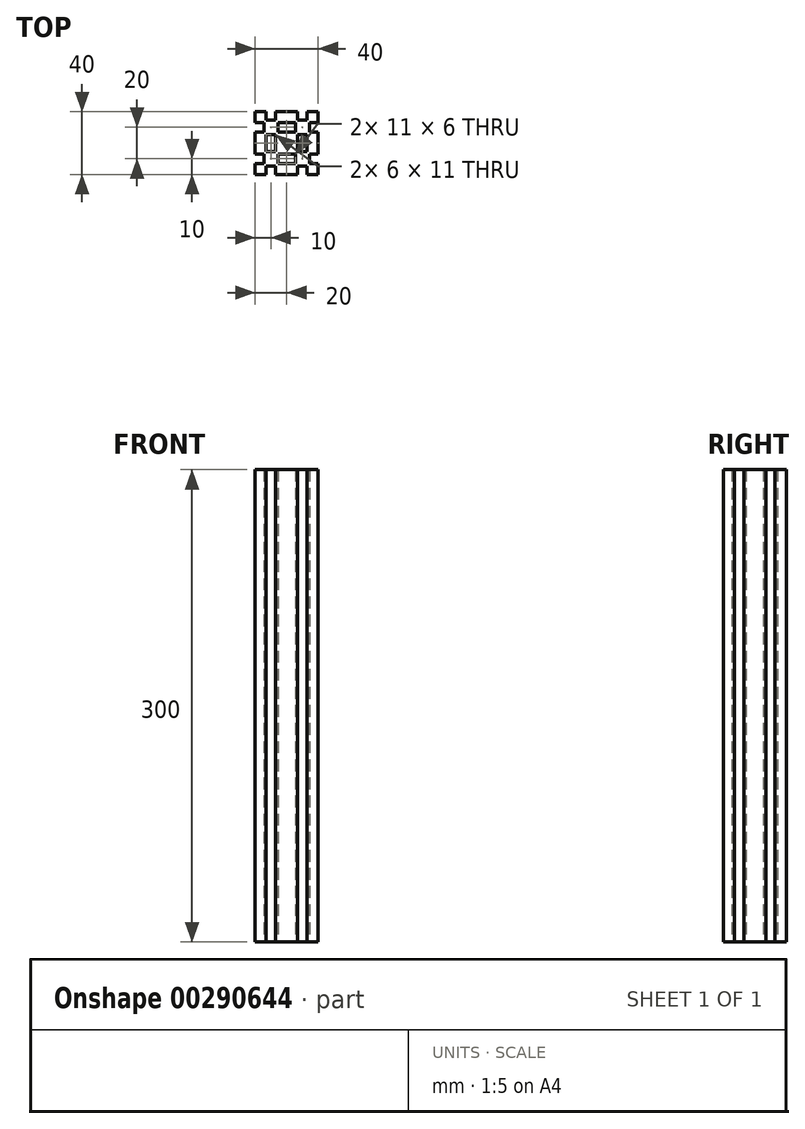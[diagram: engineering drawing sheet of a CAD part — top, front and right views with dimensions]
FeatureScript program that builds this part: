
annotation { "Feature Type Name" : "Feature", "Feature Type Description" : "" }
export const myFeature = defineFeature(function(context is Context, id is Id, definition is map)
    precondition{}
    {
        {
            var Q0;
            Q0=qCreatedBy(makeId("Top.planeOp"),FACE);
            var sketch = newSketch(context, id + "F0", { "sketchPlane" : qUnion([Q0])});
            skLineSegment(sketch, "E0.bottom", {"start": v(0, 0) * mm, "end": v(20, 0) * mm});
            skLineSegment(sketch, "E0.top", {"start": v(0, 20) * mm, "end": v(20, 20) * mm});
            skLineSegment(sketch, "E0.left", {"start": v(0, 0) * mm, "end": v(0, 20) * mm});
            skLineSegment(sketch, "E0.right", {"start": v(20, 0) * mm, "end": v(20, 20) * mm});
            skLineSegment(sketch, "E1.bottom", {"start": v(7, 20) * mm, "end": v(13, 20) * mm});
            skLineSegment(sketch, "E1.top", {"start": v(7, 14.5) * mm, "end": v(13, 14.5) * mm});
            skLineSegment(sketch, "E1.left", {"start": v(7, 20) * mm, "end": v(7, 14.5) * mm});
            skLineSegment(sketch, "E1.right", {"start": v(13, 20) * mm, "end": v(13, 14.5) * mm});
            skLineSegment(sketch, "E2.bottom", {"start": v(20, 13) * mm, "end": v(14.5, 13) * mm});
            skLineSegment(sketch, "E2.top", {"start": v(20, 7) * mm, "end": v(14.5, 7) * mm});
            skLineSegment(sketch, "E2.left", {"start": v(20, 13) * mm, "end": v(20, 7) * mm});
            skLineSegment(sketch, "E2.right", {"start": v(14.5, 13) * mm, "end": v(14.5, 7) * mm});
            skLineSegment(sketch, "E3.bottom", {"start": v(13, 0) * mm, "end": v(7, 0) * mm});
            skLineSegment(sketch, "E3.top", {"start": v(13, 5.5) * mm, "end": v(7, 5.5) * mm});
            skLineSegment(sketch, "E3.left", {"start": v(13, 0) * mm, "end": v(13, 5.5) * mm});
            skLineSegment(sketch, "E3.right", {"start": v(7, 0) * mm, "end": v(7, 5.5) * mm});
            skLineSegment(sketch, "E4.bottom", {"start": v(0, 7) * mm, "end": v(5.5, 7) * mm});
            skLineSegment(sketch, "E4.top", {"start": v(0, 13) * mm, "end": v(5.5, 13) * mm});
            skLineSegment(sketch, "E4.left", {"start": v(0, 7) * mm, "end": v(0, 13) * mm});
            skLineSegment(sketch, "E4.right", {"start": v(5.5, 7) * mm, "end": v(5.5, 13) * mm});
            skLineSegment(sketch, "E5.MirrorCS", {"start": v(-20, 13) * mm, "end": v(-14.5, 13) * mm});
            skLineSegment(sketch, "E6.MirrorCS", {"start": v(-20, 0) * mm, "end": v(-20, 20) * mm});
            skLineSegment(sketch, "E7.MirrorCS", {"start": v(-7, 20) * mm, "end": v(-7, 14.5) * mm});
            skLineSegment(sketch, "E8.MirrorCS", {"start": v(-13, 20) * mm, "end": v(-13, 14.5) * mm});
            skLineSegment(sketch, "E9.MirrorCS", {"start": v(0, 20) * mm, "end": v(-20, 20) * mm});
            skLineSegment(sketch, "E10.MirrorCS", {"start": v(-7, 20) * mm, "end": v(-13, 20) * mm});
            skLineSegment(sketch, "E11.MirrorCS", {"start": v(-20, 13) * mm, "end": v(-20, 7) * mm});
            skLineSegment(sketch, "E12.MirrorCS", {"start": v(-7, 14.5) * mm, "end": v(-13, 14.5) * mm});
            skLineSegment(sketch, "E13.MirrorCS", {"start": v(-13, 5.5) * mm, "end": v(-7, 5.5) * mm});
            skLineSegment(sketch, "E14.MirrorCS", {"start": v(0, 7) * mm, "end": v(-5.5, 7) * mm});
            skLineSegment(sketch, "E15.MirrorCS", {"start": v(-20, 7) * mm, "end": v(-14.5, 7) * mm});
            skLineSegment(sketch, "E16.MirrorCS", {"start": v(-14.5, 13) * mm, "end": v(-14.5, 7) * mm});
            skLineSegment(sketch, "E17.MirrorCS", {"start": v(-5.5, 7) * mm, "end": v(-5.5, 13) * mm});
            skLineSegment(sketch, "E18.MirrorCS", {"start": v(-7, 0) * mm, "end": v(-7, 5.5) * mm});
            skLineSegment(sketch, "E19.MirrorCS", {"start": v(-13, 0) * mm, "end": v(-7, 0) * mm});
            skLineSegment(sketch, "E20.MirrorCS", {"start": v(0, 0) * mm, "end": v(-20, 0) * mm});
            skLineSegment(sketch, "E21.MirrorCS", {"start": v(-13, 0) * mm, "end": v(-13, 5.5) * mm});
            skLineSegment(sketch, "E22.MirrorCS", {"start": v(0, 13) * mm, "end": v(-5.5, 13) * mm});
            skLineSegment(sketch, "E23.MirrorCS", {"start": v(0, -7) * mm, "end": v(0, -13) * mm});
            skLineSegment(sketch, "E24.MirrorCS", {"start": v(-20, -13) * mm, "end": v(-20, -7) * mm});
            skLineSegment(sketch, "E25.MirrorCS", {"start": v(-13, -20) * mm, "end": v(-13, -14.5) * mm});
            skLineSegment(sketch, "E26.MirrorCS", {"start": v(-7, -20) * mm, "end": v(-7, -14.5) * mm});
            skLineSegment(sketch, "E27.MirrorCS", {"start": v(-14.5, -13) * mm, "end": v(-14.5, -7) * mm});
            skLineSegment(sketch, "E28.MirrorCS", {"start": v(-7, -20) * mm, "end": v(-13, -20) * mm});
            skLineSegment(sketch, "E29.MirrorCS", {"start": v(-7, 0) * mm, "end": v(-7, -5.5) * mm});
            skLineSegment(sketch, "E30.MirrorCS", {"start": v(-20, -7) * mm, "end": v(-14.5, -7) * mm});
            skLineSegment(sketch, "E31.MirrorCS", {"start": v(0, -7) * mm, "end": v(5.5, -7) * mm});
            skLineSegment(sketch, "E32.MirrorCS", {"start": v(-13, -5.5) * mm, "end": v(-7, -5.5) * mm});
            skLineSegment(sketch, "E33.MirrorCS", {"start": v(0, -20) * mm, "end": v(-20, -20) * mm});
            skLineSegment(sketch, "E34.MirrorCS", {"start": v(20, 0) * mm, "end": v(20, -20) * mm});
            skLineSegment(sketch, "E35.MirrorCS", {"start": v(20, -13) * mm, "end": v(14.5, -13) * mm});
            skLineSegment(sketch, "E36.MirrorCS", {"start": v(0, 0) * mm, "end": v(0, -20) * mm});
            skLineSegment(sketch, "E37.MirrorCS", {"start": v(7, -20) * mm, "end": v(13, -20) * mm});
            skLineSegment(sketch, "E38.MirrorCS", {"start": v(-5.5, -7) * mm, "end": v(-5.5, -13) * mm});
            skLineSegment(sketch, "E39.MirrorCS", {"start": v(7, -20) * mm, "end": v(7, -14.5) * mm});
            skLineSegment(sketch, "E40.MirrorCS", {"start": v(13, -20) * mm, "end": v(13, -14.5) * mm});
            skLineSegment(sketch, "E41.MirrorCS", {"start": v(13, -5.5) * mm, "end": v(7, -5.5) * mm});
            skLineSegment(sketch, "E42.MirrorCS", {"start": v(0, -20) * mm, "end": v(20, -20) * mm});
            skLineSegment(sketch, "E43.MirrorCS", {"start": v(13, 0) * mm, "end": v(13, -5.5) * mm});
            skLineSegment(sketch, "E44.MirrorCS", {"start": v(-7, -14.5) * mm, "end": v(-13, -14.5) * mm});
            skLineSegment(sketch, "E45.MirrorCS", {"start": v(20, -13) * mm, "end": v(20, -7) * mm});
            skLineSegment(sketch, "E46.MirrorCS", {"start": v(14.5, -13) * mm, "end": v(14.5, -7) * mm});
            skLineSegment(sketch, "E47.MirrorCS", {"start": v(7, 0) * mm, "end": v(7, -5.5) * mm});
            skLineSegment(sketch, "E48.MirrorCS", {"start": v(0, -13) * mm, "end": v(5.5, -13) * mm});
            skLineSegment(sketch, "E49.MirrorCS", {"start": v(7, -14.5) * mm, "end": v(13, -14.5) * mm});
            skLineSegment(sketch, "E50.MirrorCS", {"start": v(-20, 0) * mm, "end": v(-20, -20) * mm});
            skLineSegment(sketch, "E51.MirrorCS", {"start": v(-13, 0) * mm, "end": v(-13, -5.5) * mm});
            skLineSegment(sketch, "E52.MirrorCS", {"start": v(20, -7) * mm, "end": v(14.5, -7) * mm});
            skLineSegment(sketch, "E53.MirrorCS", {"start": v(0, -7) * mm, "end": v(-5.5, -7) * mm});
            skLineSegment(sketch, "E54.MirrorCS", {"start": v(5.5, -7) * mm, "end": v(5.5, -13) * mm});
            skLineSegment(sketch, "E55.MirrorCS", {"start": v(0, -13) * mm, "end": v(-5.5, -13) * mm});
            skLineSegment(sketch, "E56.MirrorCS", {"start": v(-20, -13) * mm, "end": v(-14.5, -13) * mm});
            skSolve(sketch);
        }
        {
            var Q0;
            Q0=makeQuery(id+"F0.imprint","IMPRINT",FACE,{"disambiguationData":[TD([[makeQuery(id+"F0.imprint","IMPRINT",EDGE,{"derivedFrom":sQuery(id+"F0.wireOp",EDGE,"E1.top")}),-1.0]])]});
            var Q1;
            {var subQ11=sQuery(id+"F0.wireOp",EDGE,"E5.MirrorCS");Q1=makeQuery(id+"F0.imprint","IMPRINT",FACE,{"disambiguationData":[TD([[makeQuery(id+"F0.imprint","IMPRINT",EDGE,{"derivedFrom":subQ11}),1.0]])]});}
            var Q2;
            {var subQ1=sQuery(id+"F0.wireOp",EDGE,"E25.MirrorCS");Q2=makeQuery(id+"F0.imprint","IMPRINT",FACE,{"disambiguationData":[TD([[makeQuery(id+"F0.imprint","IMPRINT",EDGE,{"derivedFrom":subQ1}),1.0]])]});}
            var Q3;
            {var subQ10=sQuery(id+"F0.wireOp",EDGE,"E31.MirrorCS");Q3=makeQuery(id+"F0.imprint","IMPRINT",FACE,{"disambiguationData":[TD([[makeQuery(id+"F0.imprint","IMPRINT",EDGE,{"derivedFrom":subQ10}),1.0]])]});}
            extrude(context, id + "F1", {"entities" : qUnion([Q0, Q1, Q2, Q3]), "depth" : 300 * mm});
        }
    });
